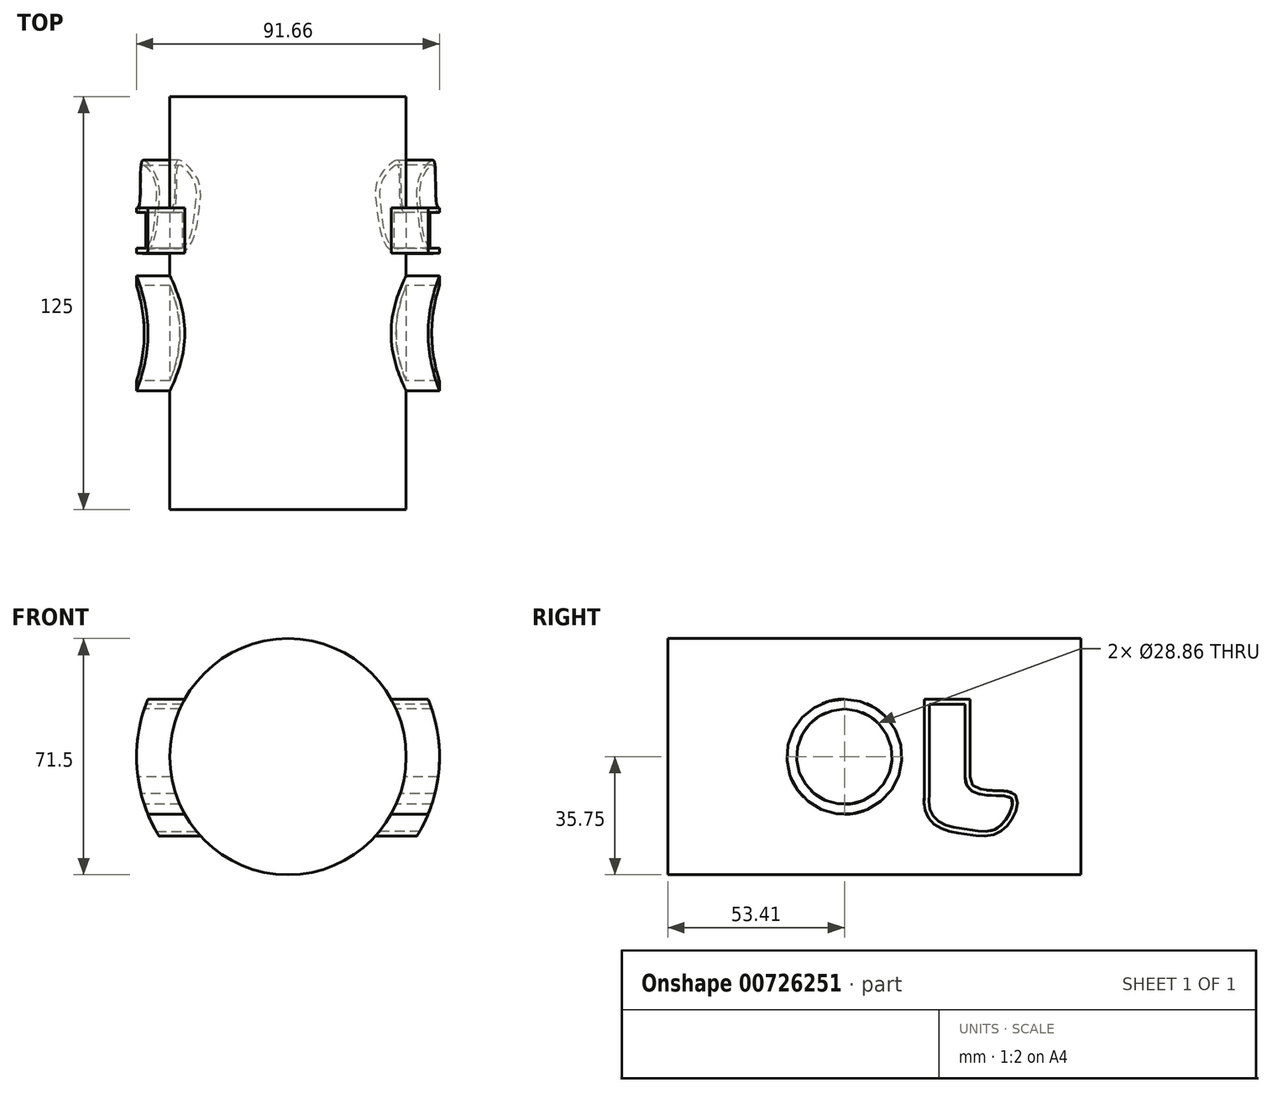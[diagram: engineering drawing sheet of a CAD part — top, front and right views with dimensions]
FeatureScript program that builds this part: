
annotation { "Feature Type Name" : "Feature", "Feature Type Description" : "" }
export const myFeature = defineFeature(function(context is Context, id is Id, definition is map)
    precondition{}
    {
        {
            var Q0;
            Q0=qCreatedBy(makeId("Front.planeOp"),FACE);
            var sketch = newSketch(context, id + "F0", { "sketchPlane" : qUnion([Q0])});
            skCircle(sketch, "E0", {"center": v(0, 0) * mm, "radius": 35.75 * mm});
            skSolve(sketch);
        }
        {
            var Q0;
            Q0 = qSketchRegion(id + "F0", true);
            extrude(context, id + "F1", {"entities" : qUnion([Q0]), "oppositeDirection" : true, "depth" : 125 * mm, "offsetDistance" : 25 * mm});
        }
        {
            var Q0;
            Q0=qCreatedBy(makeId("Right.planeOp"),FACE);
            var sketch = newSketch(context, id + "F2", { "sketchPlane" : qUnion([Q0])});
            skLineSegment(sketch, "E1", {"start": v(91.4, 17.37) * mm, "end": v(77.65, 17.37) * mm});
            skLineSegment(sketch, "E2", {"start": v(77.65, 17.37) * mm, "end": v(77.65, -11.16) * mm});
            skLineSegment(sketch, "E3", {"start": v(91.4, 17.37) * mm, "end": v(91.4, -6.13) * mm});
            skFitSpline(sketch, "E4", {"points": [v(77.65, -11.16) * mm, v(77.65, -15.38) * mm, v(81.16, -20.88) * mm, v(91.4, -23.63) * mm, v(101.4, -22.13) * mm, v(104.66, -11.16) * mm, v(91.4, -6.13) * mm], "startDerivative": vector(0, -35.95) * mm, "endDerivative": vector(0, 89.66) * mm});
            skCircle(sketch, "E5", {"center": v(53.4, 0) * mm, "radius": 17.43 * mm});
            skCircle(sketch, "E6.0", {"center": v(53.4, 0) * mm, "radius": 14.43 * mm});
            skFitSpline(sketch, "E7.0", {"points": [v(79.15, -11.16) * mm, v(79.15, -11.6) * mm, v(79.1, -12.4) * mm, v(79.02, -13.5) * mm, v(79.03, -14.34) * mm, v(79.1, -15) * mm, v(79.23, -15.69) * mm, v(79.54, -16.6) * mm, v(80.11, -17.7) * mm, v(80.76, -18.55) * mm, v(81.38, -19.16) * mm, v(81.89, -19.57) * mm, v(82.45, -19.93) * mm, v(83.09, -20.27) * mm, v(83.8, -20.56) * mm, v(84.81, -20.92) * mm, v(86.22, -21.29) * mm, v(87.75, -21.58) * mm, v(89.02, -21.78) * mm, v(89.99, -21.92) * mm, v(90.96, -22.05) * mm, v(91.94, -22.19) * mm, v(92.9, -22.32) * mm, v(94.11, -22.48) * mm, v(95.55, -22.6) * mm, v(97.1, -22.53) * mm, v(98.28, -22.25) * mm, v(99.19, -21.85) * mm, v(99.86, -21.45) * mm, v(100.53, -20.93) * mm, v(101.22, -20.25) * mm, v(101.9, -19.44) * mm, v(102.75, -18.25) * mm, v(103.47, -16.93) * mm, v(103.96, -15.65) * mm, v(104.21, -14.74) * mm, v(104.32, -13.93) * mm, v(104.3, -13.27) * mm, v(104.17, -12.81) * mm, v(104.03, -12.6) * mm, v(103.89, -12.45) * mm, v(103.75, -12.35) * mm, v(103.52, -12.24) * mm, v(103.1, -12.1) * mm, v(102.37, -11.94) * mm, v(101.28, -11.84) * mm, v(100.03, -11.78) * mm, v(98.68, -11.75) * mm, v(97.28, -11.7) * mm, v(95.87, -11.6) * mm, v(94.48, -11.38) * mm, v(93.14, -10.99) * mm, v(92.08, -10.44) * mm, v(91.32, -9.8) * mm, v(90.81, -9.23) * mm, v(90.4, -8.56) * mm, v(90.02, -7.56) * mm, v(89.9, -6.72) * mm, v(89.9, -6.13) * mm]});
            skLineSegment(sketch, "E7.1", {"start": v(79.15, 15.87) * mm, "end": v(79.15, -11.16) * mm});
            skLineSegment(sketch, "E7.2", {"start": v(89.9, 15.87) * mm, "end": v(79.15, 15.87) * mm});
            skLineSegment(sketch, "E7.3", {"start": v(89.9, 15.87) * mm, "end": v(89.9, -6.14) * mm});
            skSolve(sketch);
        }
        {
            var Q0;
            Q0 = qSketchRegion(id + "F2", true);
            extrude(context, id + "F3", {"entities" : qUnion([Q0]), "operationType" : NewBodyOperationType.ADD, "endBound" : BoundingType.SYMMETRIC, "depth" : 100 * mm, "offsetDistance" : 25 * mm});
        }
        {
            var Q0;
            Q0=qCreatedBy(makeId("Front.planeOp"),FACE);
            var sketch = newSketch(context, id + "F4", { "sketchPlane" : qUnion([Q0])});
            skCircle(sketch, "E8", {"center": v(0, 0) * mm, "radius": 45.83 * mm});
            skCircle(sketch, "E9", {"center": v(0, 0) * mm, "radius": 59.48 * mm});
            skSolve(sketch);
        }
        {
            var Q0;
            Q0=makeQuery(id+"F4.imprint","IMPRINT",FACE,{"disambiguationData":[TD([[makeQuery(id+"F4.imprint","IMPRINT",EDGE,{"derivedFrom":sQuery(id+"F4.wireOp",EDGE,"E8")}),-1.0]])]});
            extrude(context, id + "F5", {"entities" : qUnion([Q0]), "operationType" : NewBodyOperationType.REMOVE, "oppositeDirection" : true, "depth" : 125 * mm, "offsetDistance" : 25 * mm});
        }
    });
